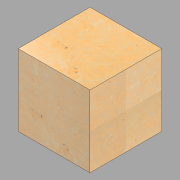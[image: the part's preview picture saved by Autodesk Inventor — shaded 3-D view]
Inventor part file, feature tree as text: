
AUTODESK INVENTOR PART (.ipt)
format: ipt  version: 2022.1 (Build 261234020, 234B)  size: 125,952 bytes
history: native  units: in
note: dims shown in document units (in); Inventor stores cm internally (conversion verified against a paired STEP export)
features: extrude x1, sketch x1
ambient origin geometry x8: Origin, YZ Plane, XZ Plane, XY Plane, X Axis, Y Axis, Z Axis, Center Point
bodies: Solid1 (feature_tree)
feature tree (2):
  extrude  "Extrusion1"  Depth=24.0in
  sketch  "Sketch1"  dims[d0=24.0in d1=24.0in d2=24.0in d3=0.0in]
